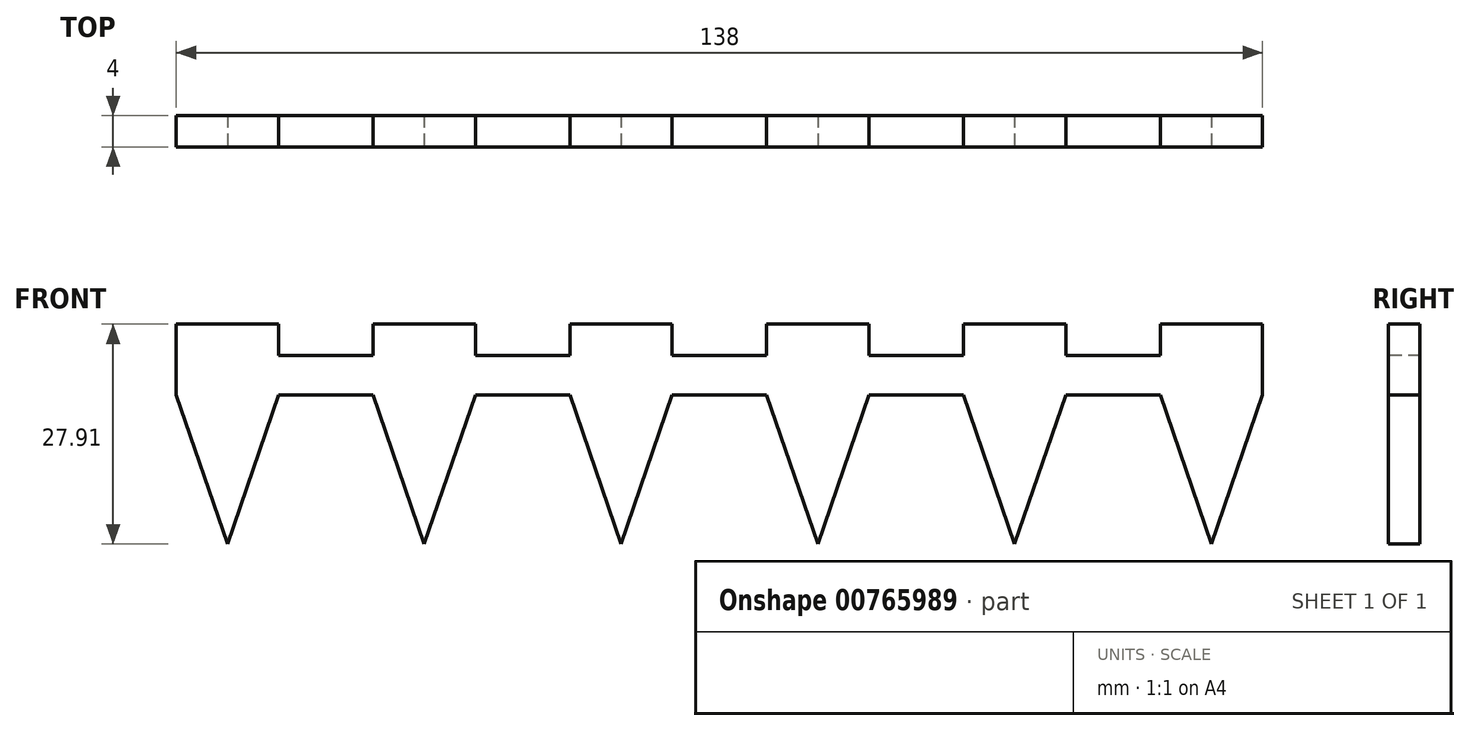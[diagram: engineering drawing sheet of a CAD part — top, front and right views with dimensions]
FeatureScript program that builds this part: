
annotation { "Feature Type Name" : "Feature", "Feature Type Description" : "" }
export const myFeature = defineFeature(function(context is Context, id is Id, definition is map)
    precondition{}
    {
        {
            var Q0;
            Q0=qCreatedBy(makeId("Top.planeOp"),FACE);
            var sketch = newSketch(context, id + "F0", { "sketchPlane" : qUnion([Q0])});
            skLineSegment(sketch, "E0.bottom", {"start": v(0, 0) * mm, "end": v(13, 0) * mm});
            skLineSegment(sketch, "E0.top", {"start": v(0, 4) * mm, "end": v(13, 4) * mm});
            skLineSegment(sketch, "E0.left", {"start": v(0, 0) * mm, "end": v(0, 4) * mm});
            skLineSegment(sketch, "E0.right", {"start": v(13, 0) * mm, "end": v(13, 4) * mm});
            skLineSegment(sketch, "E1.1.0.0", {"start": v(25, 4) * mm, "end": v(38, 4) * mm});
            skLineSegment(sketch, "E1.1.0.1", {"start": v(25, 0) * mm, "end": v(38, 0) * mm});
            skLineSegment(sketch, "E1.1.0.2", {"start": v(25, 0) * mm, "end": v(25, 4) * mm});
            skLineSegment(sketch, "E1.1.0.3", {"start": v(38, 0) * mm, "end": v(38, 4) * mm});
            skLineSegment(sketch, "E1.2.0.0", {"start": v(50, 4) * mm, "end": v(63, 4) * mm});
            skLineSegment(sketch, "E1.2.0.1", {"start": v(50, 0) * mm, "end": v(63, 0) * mm});
            skLineSegment(sketch, "E1.2.0.2", {"start": v(50, 0) * mm, "end": v(50, 4) * mm});
            skLineSegment(sketch, "E1.2.0.3", {"start": v(63, 0) * mm, "end": v(63, 4) * mm});
            skLineSegment(sketch, "E1.3.0.0", {"start": v(75, 4) * mm, "end": v(88, 4) * mm});
            skLineSegment(sketch, "E1.3.0.1", {"start": v(75, 0) * mm, "end": v(88, 0) * mm});
            skLineSegment(sketch, "E1.3.0.2", {"start": v(75, 0) * mm, "end": v(75, 4) * mm});
            skLineSegment(sketch, "E1.3.0.3", {"start": v(88, 0) * mm, "end": v(88, 4) * mm});
            skLineSegment(sketch, "E1.4.0.0", {"start": v(100, 4) * mm, "end": v(113, 4) * mm});
            skLineSegment(sketch, "E1.4.0.1", {"start": v(100, 0) * mm, "end": v(113, 0) * mm});
            skLineSegment(sketch, "E1.4.0.2", {"start": v(100, 0) * mm, "end": v(100, 4) * mm});
            skLineSegment(sketch, "E1.4.0.3", {"start": v(113, 0) * mm, "end": v(113, 4) * mm});
            skLineSegment(sketch, "E1.5.0.0", {"start": v(125, 4) * mm, "end": v(138, 4) * mm});
            skLineSegment(sketch, "E1.5.0.1", {"start": v(125, 0) * mm, "end": v(138, 0) * mm});
            skLineSegment(sketch, "E1.5.0.2", {"start": v(125, 0) * mm, "end": v(125, 4) * mm});
            skLineSegment(sketch, "E1.5.0.3", {"start": v(138, 0) * mm, "end": v(138, 4) * mm});
            skLineSegment(sketch, "E1.direction1", {"start": v(0, 0) * mm, "end": v(25, 0) * mm, "construction": true});
            skLineSegment(sketch, "E2.bottom", {"start": v(0, 4) * mm, "end": v(138, 4) * mm});
            skLineSegment(sketch, "E2.top", {"start": v(0, 0) * mm, "end": v(138, 0) * mm});
            skLineSegment(sketch, "E2.left", {"start": v(0, 4) * mm, "end": v(0, 0) * mm});
            skLineSegment(sketch, "E2.right", {"start": v(138, 4) * mm, "end": v(138, 0) * mm});
            skSolve(sketch);
        }
        {
            var Q0;
            Q0=qSketchRegion(id+"F0",true);
            extrude(context, id + "F1", {"entities" : qUnion([Q0]), "depth" : 5 * mm, "offsetDistance" : 25 * mm});
        }
        {
            var Q0;
            {var subQ0=sQuery(id+"F0.wireOp",EDGE,"E0.right");Q0=makeQuery(id+"F0.imprint","IMPRINT",FACE,{"disambiguationData":[TD([[makeQuery(id+"F0.imprint","IMPRINT",EDGE,{"derivedFrom":subQ0}),1.0]])]});}
            var Q1;
            {var subQ0=sQuery(id+"F0.wireOp",EDGE,"E1.1.0.2");Q1=makeQuery(id+"F0.imprint","IMPRINT",FACE,{"disambiguationData":[TD([[makeQuery(id+"F0.imprint","IMPRINT",EDGE,{"derivedFrom":subQ0}),-1.0]])]});}
            var Q2;
            {var subQ0=sQuery(id+"F0.wireOp",EDGE,"E1.2.0.2");Q2=makeQuery(id+"F0.imprint","IMPRINT",FACE,{"disambiguationData":[TD([[makeQuery(id+"F0.imprint","IMPRINT",EDGE,{"derivedFrom":subQ0}),-1.0]])]});}
            var Q3;
            {var subQ0=sQuery(id+"F0.wireOp",EDGE,"E1.3.0.2");Q3=makeQuery(id+"F0.imprint","IMPRINT",FACE,{"disambiguationData":[TD([[makeQuery(id+"F0.imprint","IMPRINT",EDGE,{"derivedFrom":subQ0}),-1.0]])]});}
            var Q4;
            {var subQ0=sQuery(id+"F0.wireOp",EDGE,"E1.4.0.2");Q4=makeQuery(id+"F0.imprint","IMPRINT",FACE,{"disambiguationData":[TD([[makeQuery(id+"F0.imprint","IMPRINT",EDGE,{"derivedFrom":subQ0}),-1.0]])]});}
            var Q5;
            {var subQ0=sQuery(id+"F0.wireOp",EDGE,"E1.5.0.2");Q5=makeQuery(id+"F0.imprint","IMPRINT",FACE,{"disambiguationData":[TD([[makeQuery(id+"F0.imprint","IMPRINT",EDGE,{"derivedFrom":subQ0}),-1.0]])]});}
            extrude(context, id + "F2", {"entities" : qUnion([Q0, Q1, Q2, Q3, Q4, Q5]), "operationType" : NewBodyOperationType.ADD, "depth" : 9 * mm, "offsetDistance" : 25 * mm});
        }
        {
            var Q0;
            {var subQ0=sQuery(id+"F0.wireOp",EDGE,"E2.top");Q0=makeQuery(id+"F2.boolean.opBoolean","MERGE",FACE,{"derivedFrom":[makeQuery(id+"F1.opExtrude","SWEPT_FACE",FACE,{"disambiguationData":[OSD([subQ0])]}),makeQuery(id+"F2.opExtrude","SWEPT_FACE",FACE,{"disambiguationData":[OSD([subQ0]),TDD([makeQuery(id+"F0.imprint","IMPRINT",EDGE,{"disambiguationData":[TD([[makeQuery(id+"F0.imprint","INTERSECT",VERTEX,{"derivedFrom":[sQuery(id+"F0.wireOp",EDGE,"E0.right"),subQ0]}),1.0]])],"derivedFrom":subQ0})])]}),makeQuery(id+"F2.opExtrude","SWEPT_FACE",FACE,{"disambiguationData":[OSD([subQ0]),TDD([makeQuery(id+"F0.imprint","IMPRINT",EDGE,{"disambiguationData":[TD([[makeQuery(id+"F0.imprint","INTERSECT",VERTEX,{"derivedFrom":[sQuery(id+"F0.wireOp",EDGE,"E1.1.0.2"),subQ0]}),-1.0]])],"derivedFrom":subQ0})])]}),makeQuery(id+"F2.opExtrude","SWEPT_FACE",FACE,{"disambiguationData":[OSD([subQ0]),TDD([makeQuery(id+"F0.imprint","IMPRINT",EDGE,{"disambiguationData":[TD([[makeQuery(id+"F0.imprint","INTERSECT",VERTEX,{"derivedFrom":[sQuery(id+"F0.wireOp",EDGE,"E1.2.0.2"),subQ0]}),-1.0]])],"derivedFrom":subQ0})])]}),makeQuery(id+"F2.opExtrude","SWEPT_FACE",FACE,{"disambiguationData":[OSD([subQ0]),TDD([makeQuery(id+"F0.imprint","IMPRINT",EDGE,{"disambiguationData":[TD([[makeQuery(id+"F0.imprint","INTERSECT",VERTEX,{"derivedFrom":[sQuery(id+"F0.wireOp",EDGE,"E1.3.0.2"),subQ0]}),-1.0]])],"derivedFrom":subQ0})])]}),makeQuery(id+"F2.opExtrude","SWEPT_FACE",FACE,{"disambiguationData":[OSD([subQ0]),TDD([makeQuery(id+"F0.imprint","IMPRINT",EDGE,{"disambiguationData":[TD([[makeQuery(id+"F0.imprint","INTERSECT",VERTEX,{"derivedFrom":[sQuery(id+"F0.wireOp",EDGE,"E1.4.0.2"),subQ0]}),-1.0]])],"derivedFrom":subQ0})])]}),makeQuery(id+"F2.opExtrude","SWEPT_FACE",FACE,{"disambiguationData":[OSD([subQ0]),TDD([makeQuery(id+"F0.imprint","IMPRINT",EDGE,{"disambiguationData":[TD([[makeQuery(id+"F0.imprint","INTERSECT",VERTEX,{"derivedFrom":[sQuery(id+"F0.wireOp",EDGE,"E1.5.0.2"),subQ0]}),-1.0]])],"derivedFrom":subQ0})])]})]});}
            var sketch = newSketch(context, id + "F3", { "sketchPlane" : qUnion([Q0])});
            skPoint(sketch, "E3.0", {"position": v(0, 0) * mm});
            skPoint(sketch, "E4.0", {"position": v(13, 0) * mm});
            skPoint(sketch, "E5.0", {"position": v(25, 0) * mm});
            skPoint(sketch, "E6.0", {"position": v(38, 0) * mm});
            skPoint(sketch, "E7.0", {"position": v(50, 0) * mm});
            skPoint(sketch, "E8.0", {"position": v(63, 0) * mm});
            skPoint(sketch, "E9.0", {"position": v(75, 0) * mm});
            skPoint(sketch, "E10.0", {"position": v(88, 0) * mm});
            skPoint(sketch, "E11.0", {"position": v(100, 0) * mm});
            skPoint(sketch, "E12.0", {"position": v(113, 0) * mm});
            skPoint(sketch, "E13.0", {"position": v(125, 0) * mm});
            skPoint(sketch, "E14.0", {"position": v(138, 0) * mm});
            skLineSegment(sketch, "E15", {"start": v(0, 0) * mm, "end": v(6.5, -18.91) * mm});
            skLineSegment(sketch, "E16", {"start": v(6.5, -18.91) * mm, "end": v(13, 0) * mm});
            skLineSegment(sketch, "E17", {"start": v(25, 0) * mm, "end": v(31.5, -18.91) * mm});
            skLineSegment(sketch, "E18", {"start": v(31.5, -18.91) * mm, "end": v(38, 0) * mm});
            skLineSegment(sketch, "E19", {"start": v(50, 0) * mm, "end": v(56.5, -18.91) * mm});
            skLineSegment(sketch, "E20", {"start": v(56.5, -18.91) * mm, "end": v(63, 0) * mm});
            skLineSegment(sketch, "E21", {"start": v(75, 0) * mm, "end": v(81.5, -18.91) * mm});
            skLineSegment(sketch, "E22", {"start": v(81.5, -18.91) * mm, "end": v(88, 0) * mm});
            skLineSegment(sketch, "E23", {"start": v(100, 0) * mm, "end": v(106.5, -18.91) * mm});
            skLineSegment(sketch, "E24", {"start": v(106.5, -18.91) * mm, "end": v(113, 0) * mm});
            skLineSegment(sketch, "E25", {"start": v(125, 0) * mm, "end": v(131.5, -18.91) * mm});
            skLineSegment(sketch, "E26", {"start": v(131.5, -18.91) * mm, "end": v(138, 0) * mm});
            skSolve(sketch);
        }
        {
            var Q0;
            {var subQ0=sQuery(id+"F3.wireOp",EDGE,"E15");Q0=makeQuery(id+"F3.imprint","IMPRINT",FACE,{"disambiguationData":[TD([[makeQuery(id+"F3.imprint","IMPRINT",EDGE,{"derivedFrom":subQ0}),1.0]])]});}
            var Q1;
            {var subQ0=sQuery(id+"F3.wireOp",EDGE,"E17");Q1=makeQuery(id+"F3.imprint","IMPRINT",FACE,{"disambiguationData":[TD([[makeQuery(id+"F3.imprint","IMPRINT",EDGE,{"derivedFrom":subQ0}),1.0]])]});}
            var Q2;
            {var subQ0=sQuery(id+"F3.wireOp",EDGE,"E19");Q2=makeQuery(id+"F3.imprint","IMPRINT",FACE,{"disambiguationData":[TD([[makeQuery(id+"F3.imprint","IMPRINT",EDGE,{"derivedFrom":subQ0}),1.0]])]});}
            var Q3;
            {var subQ0=sQuery(id+"F3.wireOp",EDGE,"E21");Q3=makeQuery(id+"F3.imprint","IMPRINT",FACE,{"disambiguationData":[TD([[makeQuery(id+"F3.imprint","IMPRINT",EDGE,{"derivedFrom":subQ0}),1.0]])]});}
            var Q4;
            {var subQ0=sQuery(id+"F3.wireOp",EDGE,"E23");Q4=makeQuery(id+"F3.imprint","IMPRINT",FACE,{"disambiguationData":[TD([[makeQuery(id+"F3.imprint","IMPRINT",EDGE,{"derivedFrom":subQ0}),1.0]])]});}
            var Q5;
            {var subQ0=sQuery(id+"F3.wireOp",EDGE,"E25");Q5=makeQuery(id+"F3.imprint","IMPRINT",FACE,{"disambiguationData":[TD([[makeQuery(id+"F3.imprint","IMPRINT",EDGE,{"derivedFrom":subQ0}),1.0]])]});}
            extrude(context, id + "F4", {"entities" : qUnion([Q0, Q1, Q2, Q3, Q4, Q5]), "operationType" : NewBodyOperationType.ADD, "oppositeDirection" : true, "depth" : 4 * mm, "offsetDistance" : 25 * mm});
        }
    });
